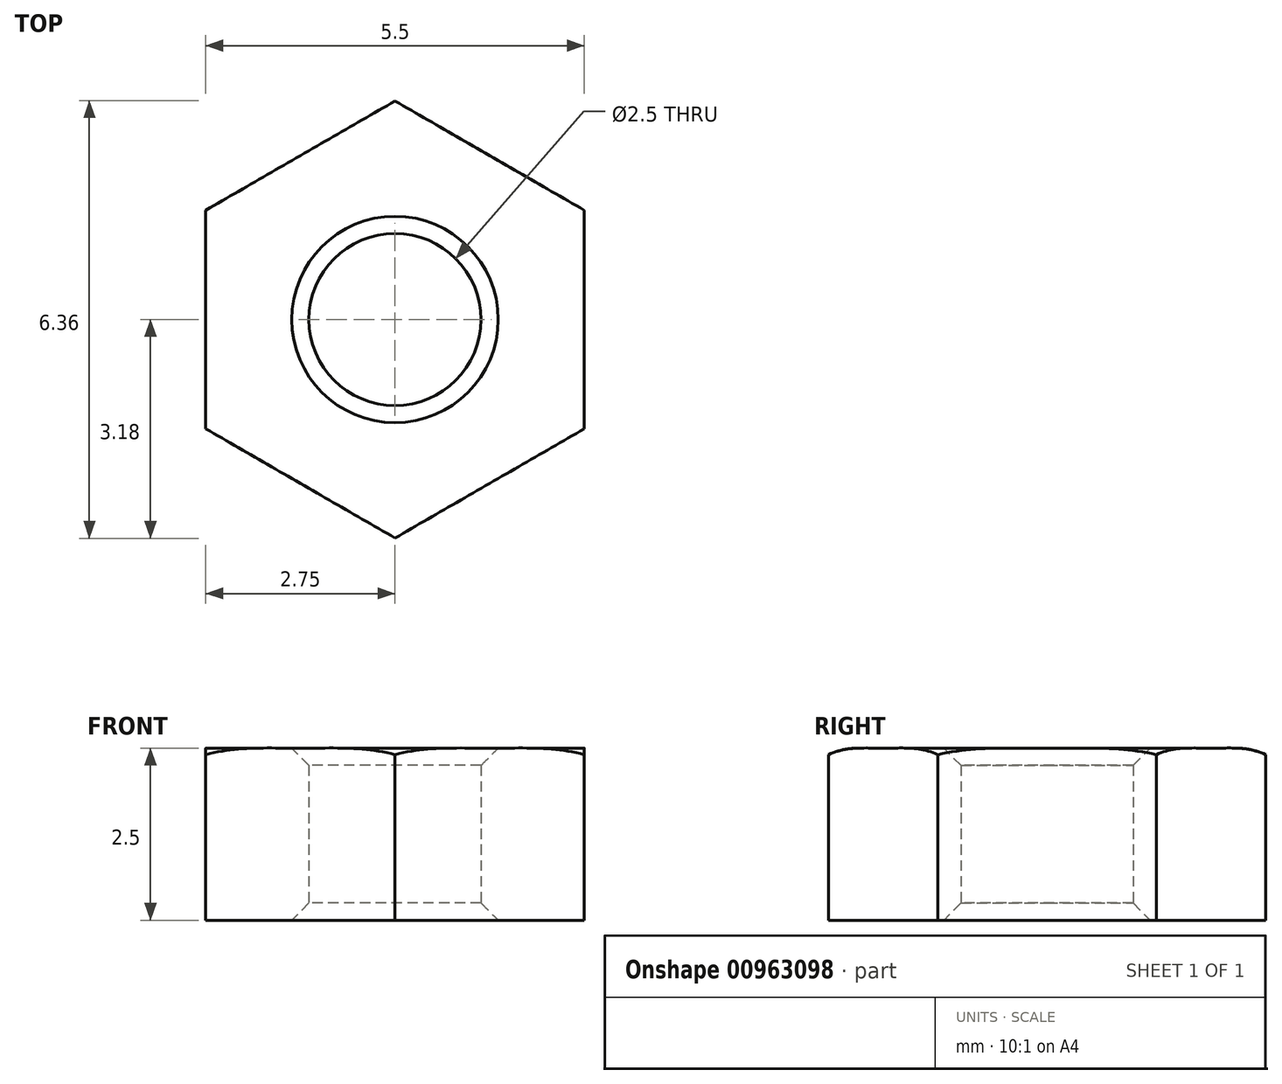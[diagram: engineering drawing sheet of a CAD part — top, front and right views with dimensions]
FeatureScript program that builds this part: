
annotation { "Feature Type Name" : "Feature", "Feature Type Description" : "" }
export const myFeature = defineFeature(function(context is Context, id is Id, definition is map)
    precondition{}
    {
        {
            var Q0;
            Q0=qCreatedBy(makeId("Top.planeOp"),FACE);
            var sketch = newSketch(context, id + "F0", { "sketchPlane" : qUnion([Q0])});
            skCircle(sketch, "E0.cCircle", {"center": v(0, 0) * mm, "radius": 2.75 * mm, "construction": true});
            skLineSegment(sketch, "E0.0", {"start": v(0, 3.18) * mm, "end": v(2.75, 1.59) * mm});
            skLineSegment(sketch, "E0.1", {"start": v(2.75, 1.59) * mm, "end": v(2.75, -1.59) * mm});
            skLineSegment(sketch, "E0.2", {"start": v(2.75, -1.59) * mm, "end": v(0, -3.18) * mm});
            skLineSegment(sketch, "E0.3", {"start": v(0, -3.18) * mm, "end": v(-2.75, -1.59) * mm});
            skLineSegment(sketch, "E0.4", {"start": v(-2.75, -1.59) * mm, "end": v(-2.75, 1.59) * mm});
            skLineSegment(sketch, "E0.5", {"start": v(-2.75, 1.59) * mm, "end": v(0, 3.18) * mm});
            skPoint(sketch, "E0.0.midPoint", {"position": v(1.38, 2.38) * mm});
            skCircle(sketch, "E1", {"center": v(0, 0) * mm, "radius": 1.25 * mm});
            skSolve(sketch);
        }
        {
            var Q0;
            Q0 = qSketchRegion(id + "F0", true);
            extrude(context, id + "F1", {"entities" : qUnion([Q0]), "depth" : 2.5 * mm, "offsetDistance" : 25 * mm, "symmetric" : true});
        }
        {
            var Q0;
            Q0=qCreatedBy(makeId("Front.planeOp"),FACE);
            var sketch = newSketch(context, id + "F2", { "sketchPlane" : qUnion([Q0])});
            skArc(sketch, "E2", {"start": v(3.65, 0.7) * mm, "mid": v(3.28, 1.1) * mm, "end": v(2.75, 1.25) * mm});
            skLineSegment(sketch, "E3", {"start": v(2.75, 1.25) * mm, "end": v(3.65, 1.25) * mm});
            skLineSegment(sketch, "E4", {"start": v(3.65, 1.25) * mm, "end": v(3.65, 0.7) * mm});
            skSolve(sketch);
        }
        {
            var Q0;
            Q0 = qSketchRegion(id + "F2", true);
            var Q1;
            Q1=makeQuery(id+"F1.opExtrude","SWEPT_FACE",FACE,{"disambiguationData":[OSD([sQuery(id+"F0.wireOp",EDGE,"E1")])]});
            revolve(context, id + "F3", {"operationType" : NewBodyOperationType.REMOVE, "surfaceOperationType" : NewSurfaceOperationType.NEW, "entities" : qUnion([Q0]), "axis" : qUnion([Q1]), "revolveType" : RevolveType.FULL, "oppositeDirection" : true});
        }
        {
            var Q0;
            Q0=makeQuery(id+"F1.opExtrude","SWEPT_FACE",FACE,{"disambiguationData":[OSD([sQuery(id+"F0.wireOp",EDGE,"E1")])]});
            chamfer(context, id + "F4", {"entities" : qUnion([Q0]), "width" : 0.25 * mm, "tangentPropagation" : true});
        }
    });
